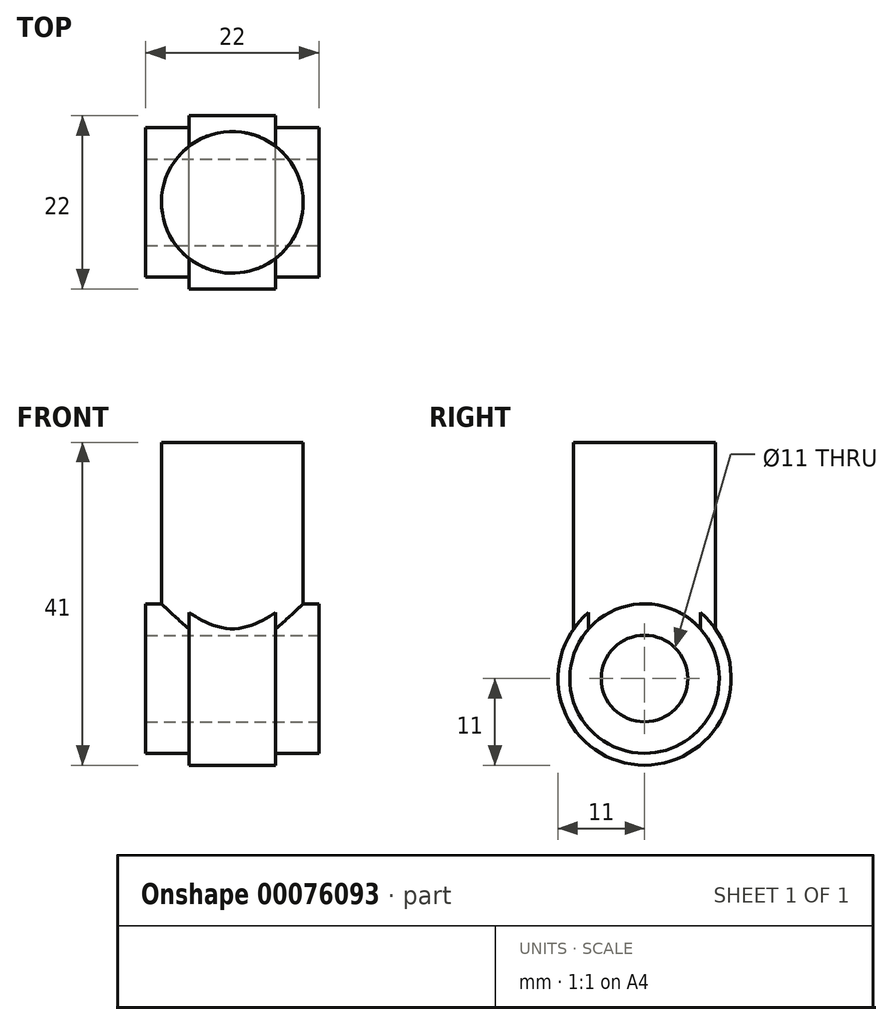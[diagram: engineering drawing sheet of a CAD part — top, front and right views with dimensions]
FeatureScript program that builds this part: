
annotation { "Feature Type Name" : "Feature", "Feature Type Description" : "" }
export const myFeature = defineFeature(function(context is Context, id is Id, definition is map)
    precondition{}
    {
        {
            var Q0;
            Q0=qCreatedBy(makeId("Right.planeOp"),FACE);
            var sketch = newSketch(context, id + "F0", { "sketchPlane" : qUnion([Q0])});
            skCircle(sketch, "E0", {"center": v(0, 0) * mm, "radius": 9.5 * mm});
            skSolve(sketch);
        }
        {
            var Q0;
            Q0=makeQuery(id+"F0.imprint","IMPRINT",FACE,{"disambiguationData":[TD([[makeQuery(id+"F0.imprint","IMPRINT",EDGE,{"derivedFrom":sQuery(id+"F0.wireOp",EDGE,"E0")}),1.0]])]});
            extrude(context, id + "F1", {"entities" : qUnion([Q0]), "endBound" : BoundingType.SYMMETRIC, "depth" : 22 * mm});
        }
        {
            var Q0;
            Q0=qCreatedBy(makeId("Top.planeOp"),FACE);
            var sketch = newSketch(context, id + "F2", { "sketchPlane" : qUnion([Q0])});
            skCircle(sketch, "E1", {"center": v(0, 0) * mm, "radius": 9 * mm});
            skSolve(sketch);
        }
        {
            var Q0;
            Q0 = qSketchRegion(id + "F2", true);
            extrude(context, id + "F3", {"entities" : qUnion([Q0]), "operationType" : NewBodyOperationType.ADD, "depth" : 30 * mm});
        }
        {
            var Q0;
            Q0=qCreatedBy(makeId("Right.planeOp"),FACE);
            cPlane(context, id + "F4", {"entities" : qUnion([Q0]), "cplaneType" : CPlaneType.OFFSET, "offset" : 13 * mm, "width" : 152.4 * mm, "height" : 152.4 * mm});
        }
        {
            var Q0;
            Q0=qCreatedBy(makeId("Right.planeOp"),FACE);
            var sketch = newSketch(context, id + "F5", { "sketchPlane" : qUnion([Q0])});
            skCircle(sketch, "E2", {"center": v(0, 0) * mm, "radius": 11 * mm});
            skSolve(sketch);
        }
        {
            var Q0;
            Q0=makeQuery(id+"F5.imprint","IMPRINT",FACE,{"disambiguationData":[TD([[makeQuery(id+"F5.imprint","IMPRINT",EDGE,{"derivedFrom":sQuery(id+"F5.wireOp",EDGE,"E2")}),1.0]])]});
            var Q1;
            Q1=sQuery(id+"F5.wireOp",EDGE,"E2");
            extrude(context, id + "F6", {"entities" : qUnion([Q0]), "operationType" : NewBodyOperationType.ADD, "surfaceEntities" : qUnion([Q1]), "endBound" : BoundingType.SYMMETRIC, "depth" : 11 * mm});
        }
        {
            var Q0;
            Q0=qCreatedBy(id+"F4.planeOp",FACE);
            var sketch = newSketch(context, id + "F7", { "sketchPlane" : qUnion([Q0])});
            skCircle(sketch, "E3", {"center": v(0, 0) * mm, "radius": 5.5 * mm});
            skSolve(sketch);
        }
        {
            var Q0;
            Q0 = qSketchRegion(id + "F7", true);
            extrude(context, id + "F8", {"entities" : qUnion([Q0]), "operationType" : NewBodyOperationType.REMOVE, "endBound" : BoundingType.SYMMETRIC, "oppositeDirection" : true, "depth" : 76.39 * mm});
        }
    });
